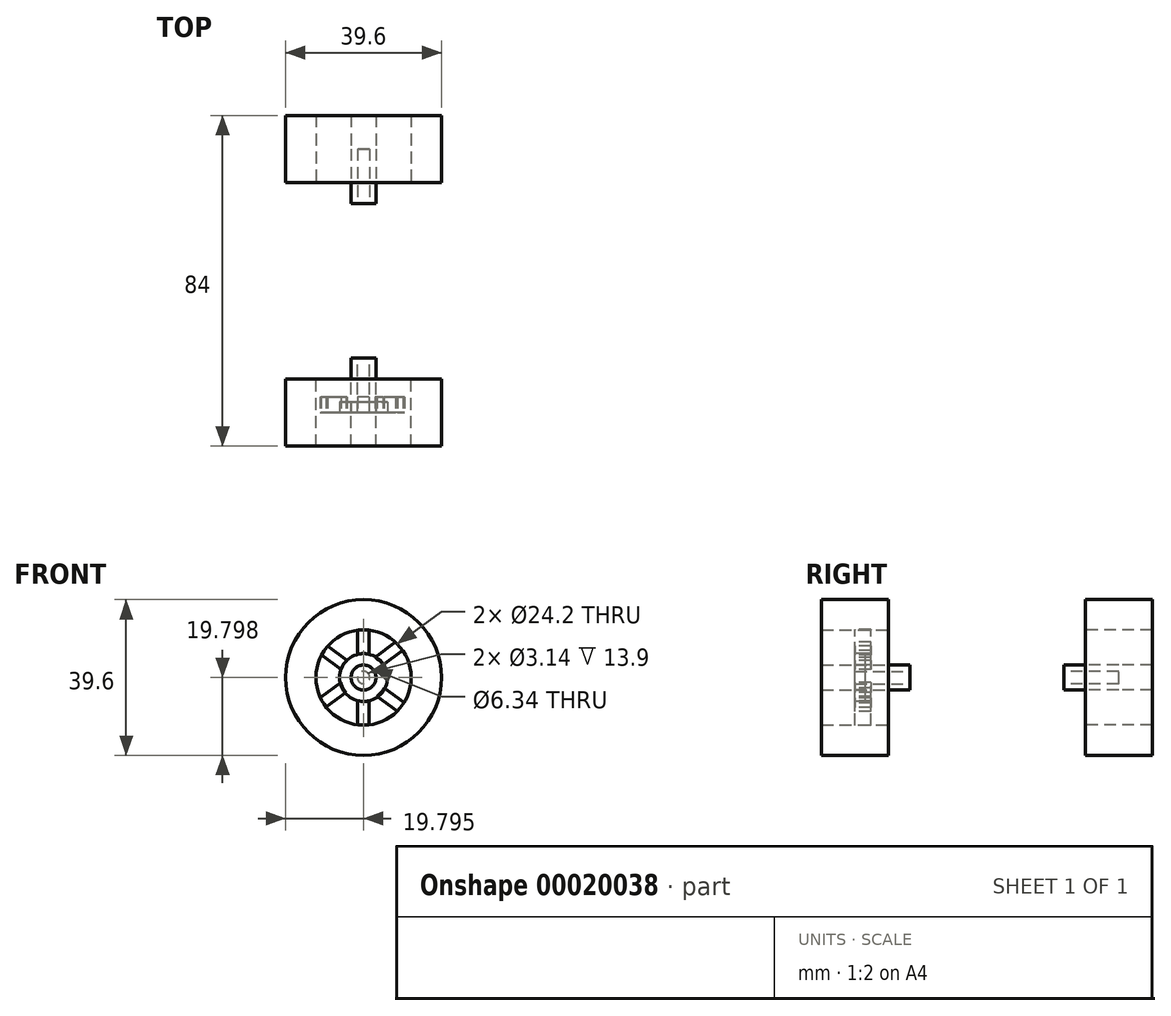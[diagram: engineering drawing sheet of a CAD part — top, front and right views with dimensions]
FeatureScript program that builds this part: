
annotation { "Feature Type Name" : "Feature", "Feature Type Description" : "" }
export const myFeature = defineFeature(function(context is Context, id is Id, definition is map)
    precondition{}
    {
        {
            var Q0;
            Q0=qCreatedBy(makeId("Front.planeOp"),FACE);
            var sketch = newSketch(context, id + "F0", { "sketchPlane" : qUnion([Q0])});
            skCircle(sketch, "E0", {"center": v(-14.5, -5.85) * mm, "radius": 3.17 * mm});
            skCircle(sketch, "E1.0", {"center": v(-14.5, -5.85) * mm, "radius": 1.57 * mm});
            skSolve(sketch);
        }
        {
            var Q0;
            Q0=makeQuery(id+"F0.imprint","IMPRINT",FACE,{"disambiguationData":[TD([[makeQuery(id+"F0.imprint","IMPRINT",EDGE,{"derivedFrom":sQuery(id+"F0.wireOp",EDGE,"E0")}),1.0]])]});
            extrude(context, id + "F1", {"entities" : qUnion([Q0]), "depth" : 9.2 * mm});
        }
        {
            var Q0;
            Q0=makeQuery(id+"F1.opExtrude","CAP_FACE",FACE,{"disambiguationData":[OSD([sQuery(id+"F0.wireOp",EDGE,"E0"),sQuery(id+"F0.wireOp",EDGE,"E1.0")])],"isStart":false});
            var sketch = newSketch(context, id + "F2", { "sketchPlane" : qUnion([Q0])});
            skCircle(sketch, "E2.0", {"center": v(-14.5, -5.85) * mm, "radius": 6.07 * mm});
            skSolve(sketch);
        }
        {
            var Q0;
            Q0=makeQuery(id+"F2.imprint","IMPRINT",FACE,{"disambiguationData":[TD([[makeQuery(id+"F2.imprint","IMPRINT",EDGE,{"derivedFrom":sQuery(id+"F2.wireOp",EDGE,"E2.0")}),1.0]])]});
            extrude(context, id + "F3", {"entities" : qUnion([Q0]), "oppositeDirection" : true, "depth" : 2.7 * mm});
        }
        {
            var Q0;
            Q0=makeQuery(id+"F3.opExtrude","CAP_FACE",FACE,{"disambiguationData":[OSD([sQuery(id+"F0.wireOp",EDGE,"E0"),sQuery(id+"F2.wireOp",EDGE,"E2.0")])],"isStart":true});
            var sketch = newSketch(context, id + "F4", { "sketchPlane" : qUnion([Q0])});
            skArc(sketch, "E3", {"start": v(-23.66, 2.2) * mm, "mid": v(-24.53, 1.09) * mm, "end": v(-25.26, -0.1) * mm});
            skLineSegment(sketch, "E4", {"start": v(-24.08, -13.4) * mm, "end": v(-19, -9.65) * mm});
            skLineSegment(sketch, "E5.0", {"start": v(-13.15, -18.05) * mm, "end": v(-13.15, -11.58) * mm});
            skLineSegment(sketch, "E6.0", {"start": v(-15.95, -18.05) * mm, "end": v(-15.95, -11.55) * mm});
            skLineSegment(sketch, "E7.0", {"start": v(-4.11, -12.26) * mm, "end": v(-9.23, -8.47) * mm});
            skLineSegment(sketch, "E8.0", {"start": v(-5.85, -14.46) * mm, "end": v(-11.04, -10.62) * mm});
            skLineSegment(sketch, "E9.0", {"start": v(-25.55, -11.01) * mm, "end": v(-20.25, -7.1) * mm});
            skLineSegment(sketch, "E10.trimOffspring", {"start": v(-13.15, -0.13) * mm, "end": v(-13.15, 6.35) * mm});
            skLineSegment(sketch, "E11.trimOffspring", {"start": v(-11.62, -0.72) * mm, "end": v(-6.32, 3.2) * mm});
            skLineSegment(sketch, "E12.trimOffspring", {"start": v(-18.55, -1.59) * mm, "end": v(-23.7, 2.22) * mm});
            skCircle(sketch, "E13", {"center": v(-14.5, -5.85) * mm, "radius": 5.88 * mm});
            skLineSegment(sketch, "E14.trimOffspring", {"start": v(-15.95, -0.15) * mm, "end": v(-15.95, 6.35) * mm});
            skLineSegment(sketch, "E15.trimOffspring", {"start": v(-20.06, -3.95) * mm, "end": v(-25.36, -0.03) * mm});
            skLineSegment(sketch, "E16.trimOffspring", {"start": v(-9.55, -2.67) * mm, "end": v(-4.46, 1.1) * mm});
            skArc(sketch, "E17.trimOffspring", {"start": v(-13.15, 6.27) * mm, "mid": v(-14.55, 6.35) * mm, "end": v(-15.95, 6.26) * mm});
            skArc(sketch, "E18.trimOffspring", {"start": v(-4.46, 1.1) * mm, "mid": v(-5.33, 2.2) * mm, "end": v(-6.32, 3.2) * mm});
            skArc(sketch, "E19.trimOffspring", {"start": v(-5.85, -14.46) * mm, "mid": v(-4.92, -13.4) * mm, "end": v(-4.11, -12.26) * mm});
            skArc(sketch, "E20.trimOffspring", {"start": v(-15.95, -17.97) * mm, "mid": v(-14.55, -18.05) * mm, "end": v(-13.15, -17.98) * mm});
            skArc(sketch, "E21.trimOffspring", {"start": v(-25.55, -11.01) * mm, "mid": v(-24.88, -12.25) * mm, "end": v(-24.08, -13.4) * mm});
            skSolve(sketch);
        }
        {
            var Q0;
            {var subQ0=sQuery(id+"F4.wireOp",EDGE,"E17.trimOffspring");Q0=makeQuery(id+"F4.imprint","IMPRINT",FACE,{"disambiguationData":[TD([[makeQuery(id+"F4.imprint","IMPRINT",EDGE,{"derivedFrom":subQ0}),1.0]])]});}
            var Q1;
            {var subQ2=sQuery(id+"F4.wireOp",EDGE,"E11.trimOffspring");Q1=makeQuery(id+"F4.imprint","IMPRINT",FACE,{"disambiguationData":[TD([[makeQuery(id+"F4.imprint","IMPRINT",EDGE,{"derivedFrom":subQ2}),-1.0]])]});}
            var Q2;
            {var subQ2=sQuery(id+"F4.wireOp",EDGE,"E7.0");Q2=makeQuery(id+"F4.imprint","IMPRINT",FACE,{"disambiguationData":[TD([[makeQuery(id+"F4.imprint","IMPRINT",EDGE,{"derivedFrom":subQ2}),1.0]])]});}
            var Q3;
            {var subQ0=sQuery(id+"F4.wireOp",EDGE,"E20.trimOffspring");Q3=makeQuery(id+"F4.imprint","IMPRINT",FACE,{"disambiguationData":[TD([[makeQuery(id+"F4.imprint","IMPRINT",EDGE,{"derivedFrom":subQ0}),1.0]])]});}
            var Q4;
            {var subQ3=sQuery(id+"F4.wireOp",EDGE,"E3");Q4=makeQuery(id+"F4.imprint","IMPRINT",FACE,{"disambiguationData":[TD([[makeQuery(id+"F4.imprint","IMPRINT",EDGE,{"derivedFrom":subQ3}),1.0]])]});}
            var Q5;
            {var subQ2=sQuery(id+"F4.wireOp",EDGE,"E4");Q5=makeQuery(id+"F4.imprint","IMPRINT",FACE,{"disambiguationData":[TD([[makeQuery(id+"F4.imprint","IMPRINT",EDGE,{"derivedFrom":subQ2}),1.0]])]});}
            extrude(context, id + "F5", {"entities" : qUnion([Q0, Q1, Q2, Q3, Q4, Q5]), "oppositeDirection" : true, "depth" : 4 * mm});
        }
        {
            var Q0;
            Q0=makeQuery(id+"F1.opExtrude","CAP_FACE",FACE,{"disambiguationData":[OSD([sQuery(id+"F0.wireOp",EDGE,"E0"),sQuery(id+"F0.wireOp",EDGE,"E1.0")])],"isStart":false});
            var sketch = newSketch(context, id + "F6", { "sketchPlane" : qUnion([Q0])});
            skCircle(sketch, "E22", {"center": v(-14.5, -5.85) * mm, "radius": 12.1 * mm});
            skCircle(sketch, "E23.0", {"center": v(-14.5, -5.85) * mm, "radius": 19.8 * mm});
            skSolve(sketch);
        }
        {
            var Q0;
            Q0=makeQuery(id+"F6.imprint","IMPRINT",FACE,{"disambiguationData":[TD([[makeQuery(id+"F6.imprint","IMPRINT",EDGE,{"derivedFrom":sQuery(id+"F6.wireOp",EDGE,"E22")}),-1.0]])]});
            extrude(context, id + "F7", {"entities" : qUnion([Q0]), "depth" : 17 * mm, "symmetric" : true});
        }
        {
            var Q0;
            Q0=makeQuery(id+"F1.opExtrude","CAP_FACE",FACE,{"disambiguationData":[OSD([sQuery(id+"F0.wireOp",EDGE,"E0"),sQuery(id+"F0.wireOp",EDGE,"E1.0")])],"isStart":true});
            extrude(context, id + "F8", {"entities" : qUnion([Q0]), "operationType" : NewBodyOperationType.ADD, "depth" : 4.7 * mm});
        }
        {
            var Q0;
            Q0=makeQuery(id+"F1.opExtrude","CAP_FACE",FACE,{"disambiguationData":[OSD([sQuery(id+"F0.wireOp",EDGE,"E0"),sQuery(id+"F0.wireOp",EDGE,"E1.0")])],"isStart":false});
            var sketch = newSketch(context, id + "F9", { "sketchPlane" : qUnion([Q0])});
            skCircle(sketch, "E24", {"center": v(-14.5, -5.85) * mm, "radius": 3.16 * mm});
            skSolve(sketch);
        }
        {
            var Q0;
            Q0 = qSketchRegion(id + "F9", true);
            var Q1;
            Q1=makeQuery(id+"F7.opExtrude","CAP_FACE",FACE,{"disambiguationData":[OSD([sQuery(id+"F6.wireOp",EDGE,"E22"),sQuery(id+"F6.wireOp",EDGE,"E23.0")])],"isStart":false});
            extrude(context, id + "F10", {"entities" : qUnion([Q0]), "operationType" : NewBodyOperationType.ADD, "endBound" : BoundingType.UP_TO_SURFACE, "endBoundEntityFace" : qUnion([Q1]), "depth" : 25 * mm});
        }
        {
            var Q0;
            Q0=makeQuery(id+"F10.opExtrude","CAP_FACE",FACE,{"disambiguationData":[OSD([sQuery(id+"F9.wireOp",EDGE,"E24")])],"isStart":false});
            extrude(context, id + "F11", {"entities" : qUnion([Q0]), "operationType" : NewBodyOperationType.ADD, "oppositeDirection" : true, "depth" : 3 * mm});
        }
        {
            var Q0;
            Q0=makeQuery(id+"F7.opExtrude","SWEPT_BODY",BODY,{"disambiguationData":[OSD([sQuery(id+"F6.wireOp",EDGE,"E22"),sQuery(id+"F6.wireOp",EDGE,"E23.0")])]});
            var Q1;
            Q1=makeQuery(id+"F1.opExtrude","SWEPT_BODY",BODY,{"disambiguationData":[OSD([sQuery(id+"F0.wireOp",EDGE,"E0"),sQuery(id+"F0.wireOp",EDGE,"E1.0")])]});
            var Q2;
            Q2=makeQuery(id+"F7.opExtrude","CAP_FACE",FACE,{"disambiguationData":[OSD([sQuery(id+"F6.wireOp",EDGE,"E22"),sQuery(id+"F6.wireOp",EDGE,"E23.0")])],"isStart":true});
            mirror(context, id + "F12", {"entities" : qUnion([Q0, Q1]), "mirrorPlane" : qUnion([Q2])});
        }
        {
            var Q0;
            Q0=makeQuery(id+"F12.opPattern","COPY",BODY,{"derivedFrom":makeQuery(id+"F1.opExtrude","SWEPT_BODY",BODY,{"disambiguationData":[OSD([sQuery(id+"F0.wireOp",EDGE,"E0"),sQuery(id+"F0.wireOp",EDGE,"E1.0")])]}),"instanceName":"1"});
            var Q1;
            Q1=makeQuery(id+"F12.opPattern","COPY",BODY,{"derivedFrom":makeQuery(id+"F7.opExtrude","SWEPT_BODY",BODY,{"disambiguationData":[OSD([sQuery(id+"F6.wireOp",EDGE,"E22"),sQuery(id+"F6.wireOp",EDGE,"E23.0")])]}),"instanceName":"1"});
            var Q2;
            Q2=makeQuery(id+"F12.opPattern","COPY",FACE,{"derivedFrom":makeQuery(id+"F10.opExtrude","SWEPT_FACE",FACE,{"disambiguationData":[OSD([sQuery(id+"F9.wireOp",EDGE,"E24")])]}),"instanceName":"1"});
            transform(context, id + "F13", {"entities" : qUnion([Q0, Q1]), "transformType" : TransformType.TRANSLATION_DISTANCE, "transformDirection" : qUnion([Q2]), "distance" : 50 * mm, "oppositeDirection" : true, "makeCopy" : false});
        }
    });
